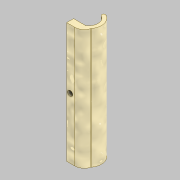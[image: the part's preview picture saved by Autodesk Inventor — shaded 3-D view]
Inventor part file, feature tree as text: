
AUTODESK INVENTOR PART (.ipt)
format: ipt  version: 2021 (Build 250183000, 183)  size: 156,160 bytes
history: native  units: mm
features: extrude x3, fillet x3, sketch x3, sweep x2, projected_geometry x2, other x2, hole x1
ambient origin geometry x8: Origin, YZ Plane, XZ Plane, XY Plane, X Axis, Y Axis, Z Axis, Center Point
bodies: Solid1 (feature_tree)
feature tree (16):
  extrude  "holderProfile"  Depth=3.665191mm
  fillet  "Fillet1"  Radius=2.0mm
  extrude  "holderBase1"  Depth=1.0mm
  fillet  "Fillet2"  Radius=1.0mm
  fillet  "Fillet3"  Radius=70.0mm
  hole  "throughHole"  [1 undecoded]
  sweep  "Sweep1"
  extrude  "Extrusion3"  Depth=1.0mm
  sketch  "Sketch1"  dims[d3=12.042772mm d4=3.665191mm d5=2.0mm]
  sketch  "Sketch2"  dims[d6=5.5mm d7=2.0mm d8=1.0mm d9=70.0mm d10=0.0mm]
  projected_geometry  "Projected Loop1"
  other  "throughholePosition"
  sweep  "sweepLine"
  other  "loopProfile"
  sketch  "Sketch7"  dims[d11=1.0mm d12=10.0mm d13=4.0mm d14=0.0mm d15=1.0mm d16=5.5mm d17=3.0mm d18=6.0mm d19=4.0mm d20=2.0mm d21=90.0deg d22=8.0mm d23=0.0mm d26=4.0mm d27=2.0mm d28=0.0mm d29=0.0mm d30=1.75mm d31=0.0mm d32=5.0mm]
  projected_geometry  "Projected Loop2"
note: 1 required parameter value undecoded (feature->parameter linkage not recoverable at this tier; creation-order binding heuristic only, values carry confidence <= 0.55)
